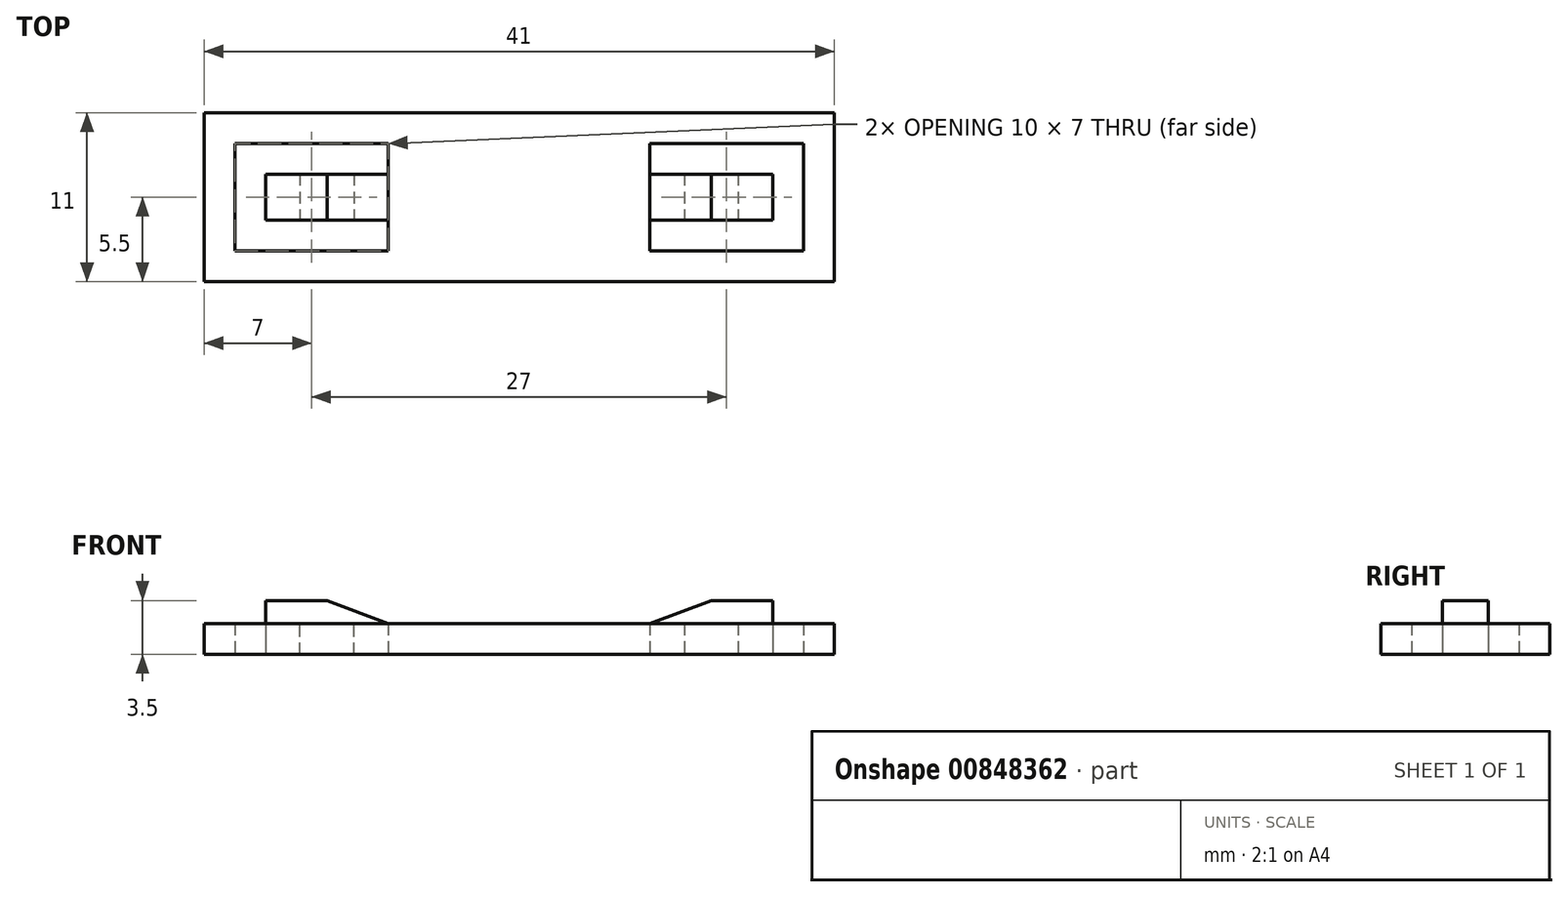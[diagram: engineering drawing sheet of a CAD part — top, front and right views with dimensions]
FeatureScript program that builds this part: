
annotation { "Feature Type Name" : "Feature", "Feature Type Description" : "" }
export const myFeature = defineFeature(function(context is Context, id is Id, definition is map)
    precondition{}
    {
        {
            var Q0;
            Q0=qCreatedBy(makeId("Top.planeOp"),FACE);
            var sketch = newSketch(context, id + "F0", { "sketchPlane" : qUnion([Q0])});
            skLineSegment(sketch, "E0", {"start": v(0, 0) * mm, "end": v(-41, 0) * mm});
            skLineSegment(sketch, "E1", {"start": v(-41, 0) * mm, "end": v(-41, -11) * mm});
            skLineSegment(sketch, "E2", {"start": v(-41, -11) * mm, "end": v(0, -11) * mm});
            skLineSegment(sketch, "E3", {"start": v(0, -11) * mm, "end": v(0, 0) * mm});
            skLineSegment(sketch, "E4", {"start": v(-39, -2) * mm, "end": v(-39, -9) * mm});
            skLineSegment(sketch, "E5", {"start": v(-39, -9) * mm, "end": v(-29, -9) * mm});
            skLineSegment(sketch, "E6", {"start": v(-29, -9) * mm, "end": v(-29, -7) * mm});
            skLineSegment(sketch, "E7", {"start": v(-29, -2) * mm, "end": v(-39, -2) * mm});
            skLineSegment(sketch, "E8", {"start": v(-37, -4) * mm, "end": v(-37, -7) * mm});
            skLineSegment(sketch, "E9", {"start": v(-37, -7) * mm, "end": v(-29, -7) * mm});
            skLineSegment(sketch, "E10", {"start": v(-37, -4) * mm, "end": v(-29, -4) * mm});
            skLineSegment(sketch, "E11.trimOffspring", {"start": v(-29, -4) * mm, "end": v(-29, -2) * mm});
            skLineSegment(sketch, "E12.MirrorCS", {"start": v(-12, -9) * mm, "end": v(-12, -7) * mm});
            skLineSegment(sketch, "E13.MirrorCS", {"start": v(-12, -4) * mm, "end": v(-12, -2) * mm});
            skLineSegment(sketch, "E14.MirrorCS", {"start": v(-4, -7) * mm, "end": v(-12, -7) * mm});
            skLineSegment(sketch, "E15.MirrorCS", {"start": v(-12, -2) * mm, "end": v(-2, -2) * mm});
            skLineSegment(sketch, "E16.MirrorCS", {"start": v(-2, -2) * mm, "end": v(-2, -9) * mm});
            skLineSegment(sketch, "E17.MirrorCS", {"start": v(-2, -9) * mm, "end": v(-12, -9) * mm});
            skLineSegment(sketch, "E18.MirrorCS", {"start": v(-4, -4) * mm, "end": v(-4, -7) * mm});
            skLineSegment(sketch, "E19.MirrorCS", {"start": v(-4, -4) * mm, "end": v(-12, -4) * mm});
            skLineSegment(sketch, "E20", {"start": v(-29, -4) * mm, "end": v(-29, -7) * mm});
            skLineSegment(sketch, "E21", {"start": v(-12, -4) * mm, "end": v(-12, -7) * mm});
            skSolve(sketch);
        }
        {
            var Q0;
            Q0 = qSketchRegion(id + "F0", true);
            extrude(context, id + "F1", {"entities" : qUnion([Q0]), "depth" : 2 * mm, "offsetDistance" : 25 * mm});
        }
        {
            var Q0;
            Q0=makeQuery(id+"F0.imprint","IMPRINT",FACE,{"disambiguationData":[TD([[makeQuery(id+"F0.imprint","IMPRINT",EDGE,{"derivedFrom":sQuery(id+"F0.wireOp",EDGE,"E8")}),1.0]])]});
            var Q1;
            Q1=makeQuery(id+"F0.imprint","IMPRINT",FACE,{"disambiguationData":[TD([[makeQuery(id+"F0.imprint","IMPRINT",EDGE,{"derivedFrom":sQuery(id+"F0.wireOp",EDGE,"E14.MirrorCS")}),-1.0]])]});
            extrude(context, id + "F2", {"entities" : qUnion([Q0, Q1]), "operationType" : NewBodyOperationType.ADD, "depth" : 3.5 * mm, "offsetDistance" : 25 * mm});
        }
        {
            var Q0;
            Q0=makeQuery(id+"F2.opExtrude","SWEPT_FACE",FACE,{"disambiguationData":[OSD([sQuery(id+"F0.wireOp",EDGE,"E9")])]});
            var sketch = newSketch(context, id + "F3", { "sketchPlane" : qUnion([Q0])});
            skLineSegment(sketch, "E22", {"start": v(-29, 2) * mm, "end": v(-33, 3.5) * mm});
            skLineSegment(sketch, "E23", {"start": v(-33, 3.5) * mm, "end": v(-29, 3.5) * mm});
            skLineSegment(sketch, "E24", {"start": v(-29, 3.5) * mm, "end": v(-29, 2) * mm});
            skLineSegment(sketch, "E25", {"start": v(-34.75, 0) * mm, "end": v(-34.75, 2) * mm});
            skLineSegment(sketch, "E26", {"start": v(-31.25, 0) * mm, "end": v(-31.25, 2) * mm});
            skLineSegment(sketch, "E27", {"start": v(-31.25, 2) * mm, "end": v(-34.75, 2) * mm});
            skLineSegment(sketch, "E28", {"start": v(-34.75, 0) * mm, "end": v(-31.25, 0) * mm});
            skSolve(sketch);
        }
        {
            var Q0;
            Q0 = qSketchRegion(id + "F3", true);
            extrude(context, id + "F4", {"entities" : qUnion([Q0]), "operationType" : NewBodyOperationType.REMOVE, "endBound" : BoundingType.UP_TO_NEXT, "oppositeDirection" : true, "depth" : 25 * mm, "offsetDistance" : 25 * mm});
        }
        {
            var Q0;
            Q0=makeQuery(id+"F2.opExtrude","SWEPT_FACE",FACE,{"disambiguationData":[OSD([sQuery(id+"F0.wireOp",EDGE,"E14.MirrorCS")])]});
            var sketch = newSketch(context, id + "F5", { "sketchPlane" : qUnion([Q0])});
            skLineSegment(sketch, "E29", {"start": v(-12, 3.5) * mm, "end": v(-12, 2) * mm});
            skLineSegment(sketch, "E30", {"start": v(-12, 2) * mm, "end": v(-8, 3.5) * mm});
            skLineSegment(sketch, "E31", {"start": v(-8, 3.5) * mm, "end": v(-12, 3.5) * mm});
            skLineSegment(sketch, "E32", {"start": v(-6.25, 0) * mm, "end": v(-6.25, 2) * mm});
            skLineSegment(sketch, "E33", {"start": v(-9.75, 0) * mm, "end": v(-9.75, 2) * mm});
            skLineSegment(sketch, "E34", {"start": v(-9.75, 2) * mm, "end": v(-6.25, 2) * mm});
            skLineSegment(sketch, "E35", {"start": v(-9.75, 0) * mm, "end": v(-6.25, 0) * mm});
            skSolve(sketch);
        }
        {
            var Q0;
            Q0 = qSketchRegion(id + "F5", true);
            extrude(context, id + "F6", {"entities" : qUnion([Q0]), "operationType" : NewBodyOperationType.REMOVE, "endBound" : BoundingType.UP_TO_NEXT, "oppositeDirection" : true, "depth" : 25 * mm, "offsetDistance" : 25 * mm});
        }
    });
